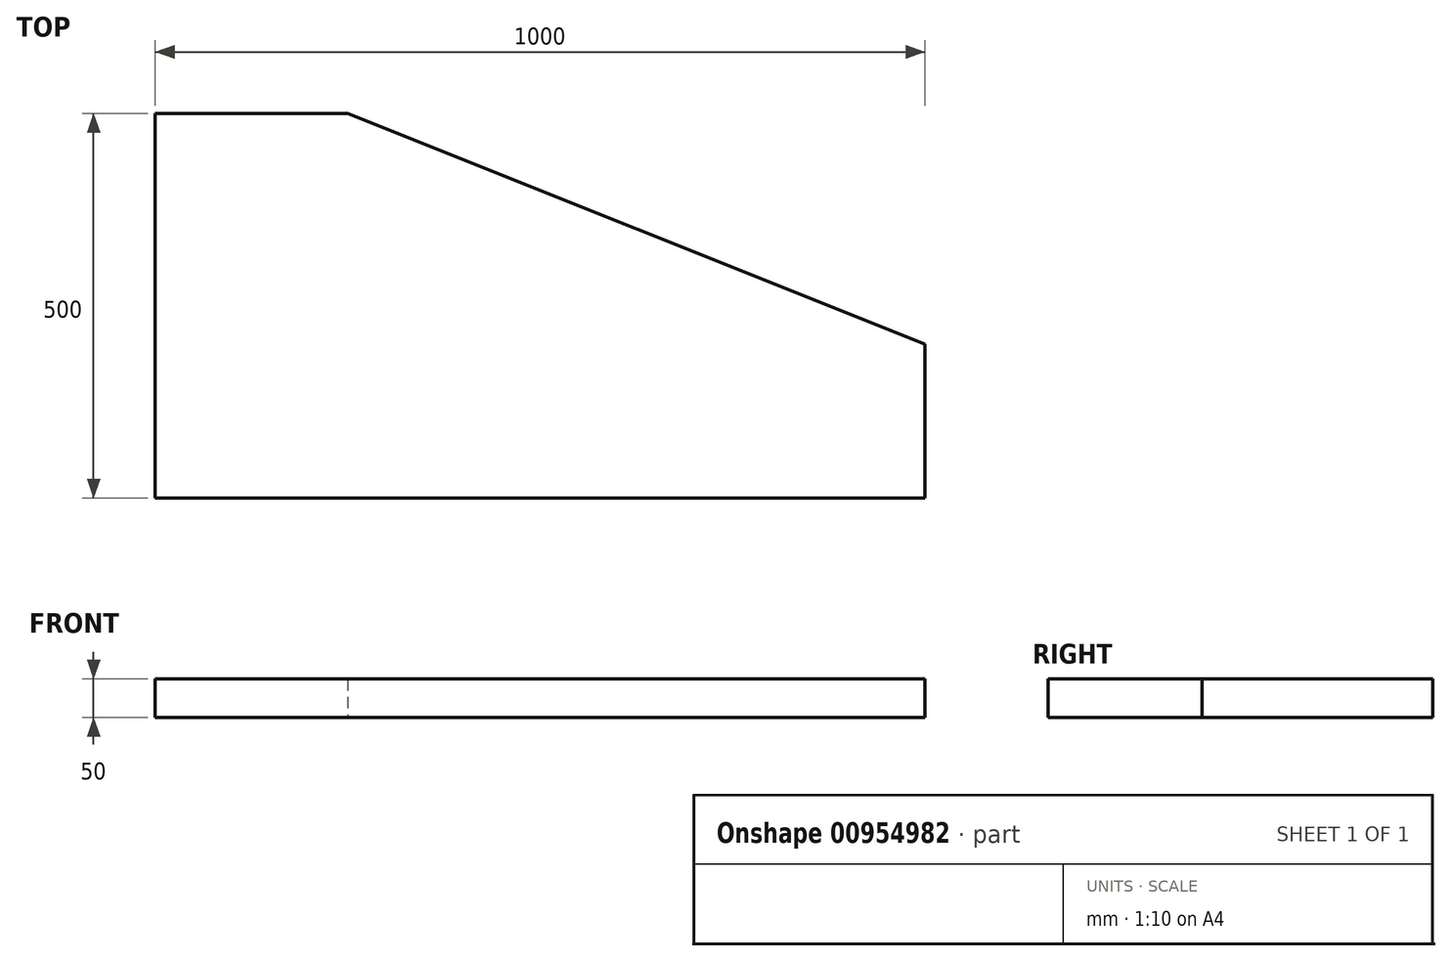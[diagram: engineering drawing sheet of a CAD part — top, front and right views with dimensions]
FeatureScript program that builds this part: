
annotation { "Feature Type Name" : "Feature", "Feature Type Description" : "" }
export const myFeature = defineFeature(function(context is Context, id is Id, definition is map)
    precondition{}
    {
        {
            var Q0;
            Q0=qCreatedBy(makeId("Top.planeOp"),FACE);
            var sketch = newSketch(context, id + "F0", { "sketchPlane" : qUnion([Q0])});
            skLineSegment(sketch, "E0", {"start": v(-233.4, 360.93) * mm, "end": v(16.6, 360.93) * mm});
            skLineSegment(sketch, "E1", {"start": v(-233.4, 360.93) * mm, "end": v(-233.4, -139.07) * mm});
            skLineSegment(sketch, "E2", {"start": v(-233.4, -139.07) * mm, "end": v(766.6, -139.07) * mm});
            skLineSegment(sketch, "E3", {"start": v(766.6, -139.07) * mm, "end": v(766.6, 60.93) * mm});
            skLineSegment(sketch, "E4", {"start": v(16.6, 360.93) * mm, "end": v(766.6, 60.93) * mm});
            skSolve(sketch);
        }
        {
            var Q0;
            Q0=makeQuery(id+"F0.imprint","IMPRINT",FACE,{"disambiguationData":[TD([[makeQuery(id+"F0.imprint","IMPRINT",EDGE,{"derivedFrom":sQuery(id+"F0.wireOp",EDGE,"E0")}),-1.0]])]});
            extrude(context, id + "F1", {"entities" : qUnion([Q0]), "depth" : 50 * mm, "offsetDistance" : 25.4 * mm});
        }
    });
